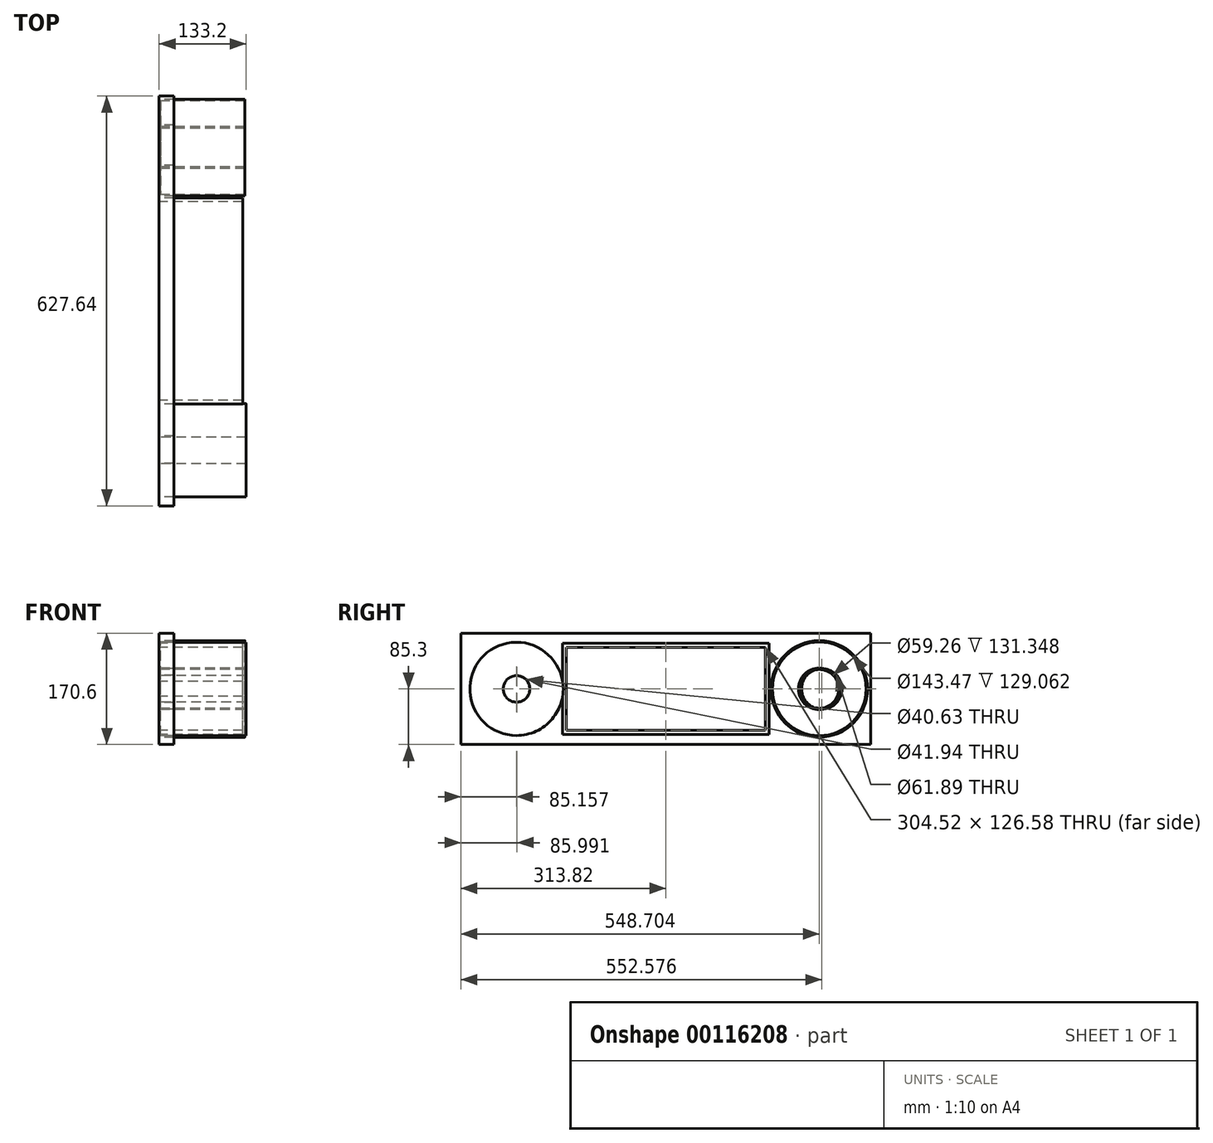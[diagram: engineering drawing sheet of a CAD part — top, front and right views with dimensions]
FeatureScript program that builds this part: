
annotation { "Feature Type Name" : "Feature", "Feature Type Description" : "" }
export const myFeature = defineFeature(function(context is Context, id is Id, definition is map)
    precondition{}
    {
        {
            var Q0;
            Q0=qCreatedBy(makeId("Right.planeOp"),FACE);
            var sketch = newSketch(context, id + "F0", { "sketchPlane" : qUnion([Q0])});
            skLineSegment(sketch, "E0.bottom", {"start": v(228.6, -76.2) * mm, "end": v(-228.6, -76.2) * mm});
            skLineSegment(sketch, "E0.right", {"start": v(-228.6, -76.2) * mm, "end": v(-228.6, -73.76) * mm});
            skPoint(sketch, "E0.middle", {"position": v(0, 0) * mm});
            skArc(sketch, "E1", {"start": v(-228.6, 73.76) * mm, "mid": v(-302.36, 0) * mm, "end": v(-228.6, -73.76) * mm});
            skArc(sketch, "E2", {"start": v(228.6, -76.2) * mm, "mid": v(304.8, 0) * mm, "end": v(228.6, 76.2) * mm});
            skCircle(sketch, "E3", {"center": v(228.6, 0) * mm, "radius": 25.76 * mm});
            skCircle(sketch, "E4", {"center": v(-228.6, 0) * mm, "radius": 18.97 * mm});
            skLineSegment(sketch, "E5.trimOffspring", {"start": v(-228.6, 73.76) * mm, "end": v(-228.6, 76.2) * mm});
            skLineSegment(sketch, "E6", {"start": v(228.6, 76.2) * mm, "end": v(228.6, -76.2) * mm});
            skLineSegment(sketch, "E7", {"start": v(-228.6, 73.76) * mm, "end": v(228.6, 76.2) * mm});
            skSolve(sketch);
        }
        {
            var Q0;
            Q0=sQuery(id+"F0.wireOp",EDGE,"E2");
            var Q1;
            Q1=sQuery(id+"F0.wireOp",EDGE,"E0.bottom");
            var Q2;
            Q2=sQuery(id+"F0.wireOp",EDGE,"E7");
            var Q3;
            Q3=sQuery(id+"F0.wireOp",EDGE,"E1");
            extrude(context, id + "F1", {"bodyType" : ToolBodyType.SURFACE, "surfaceEntities" : qUnion([Q0, Q1, Q2, Q3]), "depth" : 0.15 * yard});
        }
        {
            var Q0;
            Q0=qCreatedBy(makeId("Right.planeOp"),FACE);
            var sketch = newSketch(context, id + "F2", { "sketchPlane" : qUnion([Q0])});
            skLineSegment(sketch, "E8", {"start": v(0, 0) * mm, "end": v(-299.7, 0) * mm});
            skCircle(sketch, "E9", {"center": v(-228.66, 0) * mm, "radius": 71.45 * mm});
            skCircle(sketch, "E10", {"center": v(-228.66, 0) * mm, "radius": 20.31 * mm});
            skSolve(sketch);
        }
        {
            var Q0;
            Q0 = qSketchRegion(id + "F2", true);
            extrude(context, id + "F3", {"entities" : qUnion([Q0]), "depth" : 0.15 * yard});
        }
        {
            var Q0;
            Q0=qCreatedBy(makeId("Right.planeOp"),FACE);
            var sketch = newSketch(context, id + "F4", { "sketchPlane" : qUnion([Q0])});
            skLineSegment(sketch, "E11", {"start": v(74.47, 0) * mm, "end": v(303.5, 0) * mm});
            skCircle(sketch, "E12", {"center": v(234.88, 0) * mm, "radius": 74.02 * mm});
            skCircle(sketch, "E13", {"center": v(234.88, 0) * mm, "radius": 29.63 * mm});
            skSolve(sketch);
        }
        {
            var Q0;
            Q0=makeQuery(id+"F4.imprint","IMPRINT",FACE,{"disambiguationData":[TD([[makeQuery(id+"F4.imprint","IMPRINT",EDGE,{"derivedFrom":sQuery(id+"F4.wireOp",EDGE,"E12")}),1.0]])]});
            extrude(context, id + "F5", {"entities" : qUnion([Q0]), "depth" : 0.14 * yard});
        }
        {
            var Q0;
            Q0=qCreatedBy(makeId("Right.planeOp"),FACE);
            var sketch = newSketch(context, id + "F6", { "sketchPlane" : qUnion([Q0])});
            skLineSegment(sketch, "E14.bottom", {"start": v(152.26, -63.3) * mm, "end": v(-152.26, -63.3) * mm});
            skLineSegment(sketch, "E14.top", {"start": v(152.26, 63.3) * mm, "end": v(-152.26, 63.3) * mm});
            skLineSegment(sketch, "E14.left", {"start": v(152.26, -63.3) * mm, "end": v(152.26, 63.3) * mm});
            skLineSegment(sketch, "E14.right", {"start": v(-152.26, -63.3) * mm, "end": v(-152.26, 63.3) * mm});
            skPoint(sketch, "E14.middle", {"position": v(0, 0) * mm});
            skSolve(sketch);
        }
        {
            var Q0;
            Q0=makeQuery(id+"F6.imprint","IMPRINT",FACE,{"disambiguationData":[TD([[makeQuery(id+"F6.imprint","IMPRINT",EDGE,{"derivedFrom":sQuery(id+"F6.wireOp",EDGE,"E14.bottom")}),-1.0]])]});
            var sketch = newSketch(context, id + "F7", { "sketchPlane" : qUnion([Q0])});
            skLineSegment(sketch, "E15.bottom", {"start": v(158.1, -70) * mm, "end": v(-158.1, -70) * mm});
            skLineSegment(sketch, "E15.top", {"start": v(158.1, 70) * mm, "end": v(-158.1, 70) * mm});
            skLineSegment(sketch, "E15.left", {"start": v(158.1, -70) * mm, "end": v(158.1, 70) * mm});
            skLineSegment(sketch, "E15.right", {"start": v(-158.1, -70) * mm, "end": v(-158.1, 70) * mm});
            skPoint(sketch, "E15.middle", {"position": v(0, 0) * mm});
            skSolve(sketch);
        }
        {
            var Q0;
            Q0=makeQuery(id+"F7.imprint","IMPRINT",FACE,{"disambiguationData":[TD([[makeQuery(id+"F7.imprint","IMPRINT",EDGE,{"derivedFrom":sQuery(id+"F7.wireOp",EDGE,"E15.bottom")}),-1.0]])]});
            var Q1;
            Q1=sQuery(id+"F6.wireOp",EDGE,"E14.left");
            var Q2;
            Q2=sQuery(id+"F6.wireOp",EDGE,"E14.right");
            var Q3;
            Q3=sQuery(id+"F6.wireOp",EDGE,"E14.bottom");
            var Q4;
            Q4=sQuery(id+"F7.wireOp",EDGE,"E15.left");
            var Q5;
            Q5=sQuery(id+"F6.wireOp",EDGE,"E14.top");
            var Q6;
            Q6=sQuery(id+"F7.wireOp",EDGE,"E15.bottom");
            var Q7;
            Q7=sQuery(id+"F7.wireOp",EDGE,"E15.right");
            var Q8;
            Q8=sQuery(id+"F7.wireOp",EDGE,"E15.top");
            extrude(context, id + "F8", {"entities" : qUnion([Q0]), "operationType" : NewBodyOperationType.ADD, "surfaceEntities" : qUnion([Q1, Q2, Q3, Q4, Q5, Q6, Q7, Q8]), "depth" : 0.14 * yard});
        }
        {
            var Q0;
            Q0=qCreatedBy(makeId("Right.planeOp"),FACE);
            var sketch = newSketch(context, id + "F9", { "sketchPlane" : qUnion([Q0])});
            skLineSegment(sketch, "E16.bottom", {"start": v(-154.17, -7.5) * mm, "end": v(-156.98, -7.5) * mm});
            skLineSegment(sketch, "E16.top", {"start": v(-154.17, 7.5) * mm, "end": v(-156.98, 7.5) * mm});
            skLineSegment(sketch, "E16.left", {"start": v(-154.17, -7.5) * mm, "end": v(-154.17, 7.5) * mm});
            skLineSegment(sketch, "E16.right", {"start": v(-156.98, -7.5) * mm, "end": v(-156.98, 7.5) * mm});
            skPoint(sketch, "E16.middle", {"position": v(-155.57, 0) * mm});
            skSolve(sketch);
        }
        {
            var Q0;
            Q0 = qSketchRegion(id + "F9", true);
            extrude(context, id + "F10", {"entities" : qUnion([Q0]), "operationType" : NewBodyOperationType.ADD, "depth" : 0.03 * yard});
        }
        {
            var Q0;
            Q0=qCreatedBy(makeId("Right.planeOp"),FACE);
            var sketch = newSketch(context, id + "F11", { "sketchPlane" : qUnion([Q0])});
            skLineSegment(sketch, "E17.bottom", {"start": v(313.82, -85.3) * mm, "end": v(-313.82, -85.3) * mm});
            skLineSegment(sketch, "E17.top", {"start": v(313.82, 85.3) * mm, "end": v(-313.82, 85.3) * mm});
            skLineSegment(sketch, "E17.left", {"start": v(313.82, -85.3) * mm, "end": v(313.82, 85.3) * mm});
            skLineSegment(sketch, "E17.right", {"start": v(-313.82, -85.3) * mm, "end": v(-313.82, 85.3) * mm});
            skPoint(sketch, "E17.middle", {"position": v(0, 0) * mm});
            skCircle(sketch, "E18", {"center": v(-227.83, 0) * mm, "radius": 20.97 * mm});
            skCircle(sketch, "E19", {"center": v(238.76, 0) * mm, "radius": 30.94 * mm});
            skSolve(sketch);
        }
        {
            var Q0;
            Q0=makeQuery(id+"F11.imprint","IMPRINT",FACE,{"disambiguationData":[TD([[makeQuery(id+"F11.imprint","IMPRINT",EDGE,{"derivedFrom":sQuery(id+"F11.wireOp",EDGE,"E17.bottom")}),-1.0]])]});
            extrude(context, id + "F12", {"entities" : qUnion([Q0]), "depth" : 0.03 * yard});
        }
        {
            var Q0;
            Q0=makeQuery(id+"F5.opExtrude","CAP_FACE",FACE,{"disambiguationData":[OSD([sQuery(id+"F4.wireOp",EDGE,"E12"),sQuery(id+"F4.wireOp",EDGE,"E13")])],"isStart":false});
            shell(context, id + "F13", {"entities" : qUnion([Q0]), "thickness" : 0 * yard});
        }
    });
